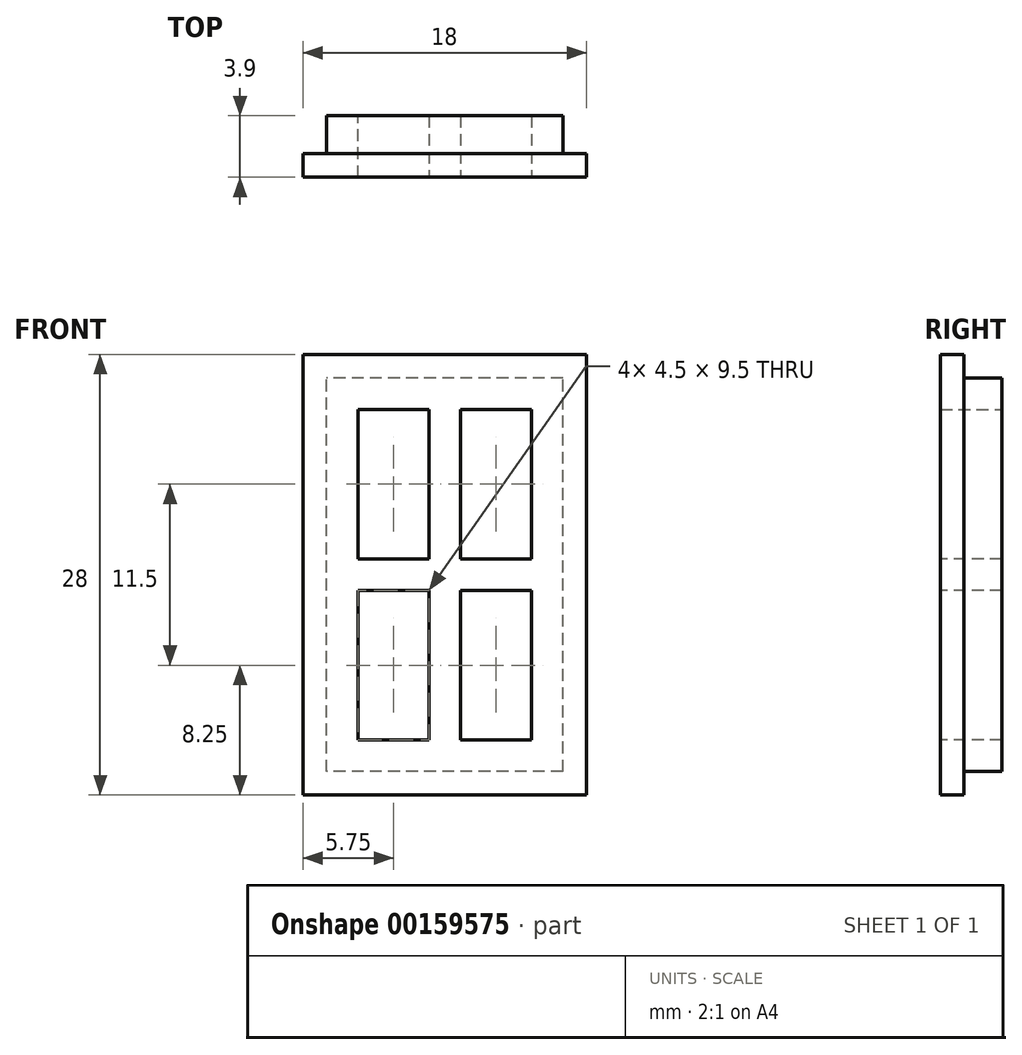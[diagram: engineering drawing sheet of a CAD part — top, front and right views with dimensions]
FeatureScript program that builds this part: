
annotation { "Feature Type Name" : "Feature", "Feature Type Description" : "" }
export const myFeature = defineFeature(function(context is Context, id is Id, definition is map)
    precondition{}
    {
        {
            var Q0;
            Q0=qCreatedBy(makeId("Front.planeOp"),FACE);
            var sketch = newSketch(context, id + "F0", { "sketchPlane" : qUnion([Q0])});
            skLineSegment(sketch, "E0.bottom", {"start": v(7.5, -12.5) * mm, "end": v(-7.5, -12.5) * mm});
            skLineSegment(sketch, "E0.top", {"start": v(7.5, 12.5) * mm, "end": v(-7.5, 12.5) * mm});
            skLineSegment(sketch, "E0.left", {"start": v(7.5, -12.5) * mm, "end": v(7.5, 12.5) * mm});
            skLineSegment(sketch, "E0.right", {"start": v(-7.5, -12.5) * mm, "end": v(-7.5, 12.5) * mm});
            skPoint(sketch, "E0.middle", {"position": v(0, 0) * mm});
            skLineSegment(sketch, "E1.0", {"start": v(5.5, -10.5) * mm, "end": v(5.5, 10.5) * mm});
            skLineSegment(sketch, "E1.1", {"start": v(5.5, -10.5) * mm, "end": v(-5.5, -10.5) * mm});
            skLineSegment(sketch, "E1.2", {"start": v(-5.5, -10.5) * mm, "end": v(-5.5, 10.5) * mm});
            skLineSegment(sketch, "E1.3", {"start": v(5.5, 10.5) * mm, "end": v(-5.5, 10.5) * mm});
            skSolve(sketch);
        }
        {
            var Q0;
            Q0=makeQuery(id+"F0.imprint","IMPRINT",FACE,{"disambiguationData":[TD([[makeQuery(id+"F0.imprint","IMPRINT",EDGE,{"derivedFrom":sQuery(id+"F0.wireOp",EDGE,"E0.bottom")}),-1.0]])]});
            extrude(context, id + "F1", {"entities" : qUnion([Q0]), "depth" : 2.4 * mm});
        }
        {
            var Q0;
            Q0=makeQuery(id+"F1.opExtrude","CAP_FACE",FACE,{"disambiguationData":[OSD([sQuery(id+"F0.wireOp",EDGE,"E0.bottom"),sQuery(id+"F0.wireOp",EDGE,"E0.top"),sQuery(id+"F0.wireOp",EDGE,"E0.left"),sQuery(id+"F0.wireOp",EDGE,"E0.right"),sQuery(id+"F0.wireOp",EDGE,"E1.0"),sQuery(id+"F0.wireOp",EDGE,"E1.1"),sQuery(id+"F0.wireOp",EDGE,"E1.2"),sQuery(id+"F0.wireOp",EDGE,"E1.3")])],"isStart":false});
            var sketch = newSketch(context, id + "F2", { "sketchPlane" : qUnion([Q0])});
            skLineSegment(sketch, "E2.0", {"start": v(5.5, 10.5) * mm, "end": v(-5.5, 10.5) * mm});
            skLineSegment(sketch, "E3.0", {"start": v(-5.5, -10.5) * mm, "end": v(-5.5, 10.5) * mm});
            skLineSegment(sketch, "E4.0", {"start": v(5.5, -10.5) * mm, "end": v(5.5, 10.5) * mm});
            skLineSegment(sketch, "E5.0", {"start": v(5.5, -10.5) * mm, "end": v(-5.5, -10.5) * mm});
            skLineSegment(sketch, "E6.bottom", {"start": v(9, -14) * mm, "end": v(-9, -14) * mm});
            skLineSegment(sketch, "E6.top", {"start": v(9, 14) * mm, "end": v(-9, 14) * mm});
            skLineSegment(sketch, "E6.left", {"start": v(9, -14) * mm, "end": v(9, 14) * mm});
            skLineSegment(sketch, "E6.right", {"start": v(-9, -14) * mm, "end": v(-9, 14) * mm});
            skPoint(sketch, "E6.middle", {"position": v(0, 0) * mm});
            skSolve(sketch);
        }
        {
            var Q0;
            Q0=makeQuery(id+"F2.imprint","IMPRINT",FACE,{"disambiguationData":[TD([[makeQuery(id+"F2.imprint","IMPRINT",EDGE,{"derivedFrom":sQuery(id+"F2.wireOp",EDGE,"E2.0")}),-1.0]])]});
            var Q1;
            Q1=makeQuery(id+"F2.imprint","IMPRINT",FACE,{"disambiguationData":[TD([[makeQuery(id+"F2.imprint","IMPRINT",EDGE,{"derivedFrom":sQuery(id+"F2.wireOp",EDGE,"E6.bottom")}),-1.0]])]});
            extrude(context, id + "F3", {"entities" : qUnion([Q0, Q1]), "operationType" : NewBodyOperationType.ADD, "depth" : 1.5 * mm});
        }
        {
            var Q0;
            Q0=makeQuery(id+"F3.opExtrude","CAP_FACE",FACE,{"disambiguationData":[OSD([sQuery(id+"F2.wireOp",EDGE,"E2.0"),sQuery(id+"F2.wireOp",EDGE,"E3.0"),sQuery(id+"F2.wireOp",EDGE,"E4.0"),sQuery(id+"F2.wireOp",EDGE,"E5.0"),sQuery(id+"F2.wireOp",EDGE,"E6.bottom"),sQuery(id+"F2.wireOp",EDGE,"E6.top"),sQuery(id+"F2.wireOp",EDGE,"E6.left"),sQuery(id+"F2.wireOp",EDGE,"E6.right")])],"isStart":false});
            var sketch = newSketch(context, id + "F4", { "sketchPlane" : qUnion([Q0])});
            skLineSegment(sketch, "E7.bottom", {"start": v(-1, 10.5) * mm, "end": v(1, 10.5) * mm});
            skLineSegment(sketch, "E7.top", {"start": v(-1, -10.5) * mm, "end": v(1, -10.5) * mm});
            skLineSegment(sketch, "E7.left", {"start": v(-1, 10.5) * mm, "end": v(-1, -10.5) * mm});
            skLineSegment(sketch, "E7.right", {"start": v(1, 10.5) * mm, "end": v(1, -10.5) * mm});
            skLineSegment(sketch, "E8.bottom", {"start": v(-5.5, 1) * mm, "end": v(5.5, 1) * mm});
            skLineSegment(sketch, "E8.top", {"start": v(-5.5, -1) * mm, "end": v(5.5, -1) * mm});
            skLineSegment(sketch, "E8.left", {"start": v(-5.5, 1) * mm, "end": v(-5.5, -1) * mm});
            skLineSegment(sketch, "E8.right", {"start": v(5.5, 1) * mm, "end": v(5.5, -1) * mm});
            skPoint(sketch, "E9", {"position": v(0, 10.5) * mm});
            skPoint(sketch, "E10", {"position": v(5.5, 0) * mm});
            skSolve(sketch);
        }
        {
            var Q0;
            {var subQ5=sQuery(id+"F4.wireOp",EDGE,"E8.left");Q0=makeQuery(id+"F4.imprint","IMPRINT",FACE,{"disambiguationData":[TD([[makeQuery(id+"F4.imprint","IMPRINT",EDGE,{"derivedFrom":subQ5}),-1.0]])]});}
            var Q1;
            {var subQ0=sQuery(id+"F4.wireOp",EDGE,"E7.bottom");Q1=makeQuery(id+"F4.imprint","IMPRINT",FACE,{"disambiguationData":[TD([[makeQuery(id+"F4.imprint","IMPRINT",EDGE,{"derivedFrom":subQ0}),1.0]])]});}
            var Q2;
            {var subQ0=sQuery(id+"F4.wireOp",EDGE,"E8.bottom");var subQ1=sQuery(id+"F4.wireOp",EDGE,"E7.left");var subQ2=makeQuery(id+"F4.imprint","INTERSECT",VERTEX,{"derivedFrom":[subQ1,subQ0]});Q2=makeQuery(id+"F4.imprint","IMPRINT",FACE,{"disambiguationData":[TD([[makeQuery(id+"F4.imprint","IMPRINT",EDGE,{"disambiguationData":[TD([[subQ2,-1.0]])],"derivedFrom":subQ1}),1.0]])]});}
            var Q3;
            {var subQ5=sQuery(id+"F4.wireOp",EDGE,"E8.right");Q3=makeQuery(id+"F4.imprint","IMPRINT",FACE,{"disambiguationData":[TD([[makeQuery(id+"F4.imprint","IMPRINT",EDGE,{"derivedFrom":subQ5}),1.0]])]});}
            var Q4;
            {var subQ0=sQuery(id+"F4.wireOp",EDGE,"E7.top");Q4=makeQuery(id+"F4.imprint","IMPRINT",FACE,{"disambiguationData":[TD([[makeQuery(id+"F4.imprint","IMPRINT",EDGE,{"derivedFrom":subQ0}),-1.0]])]});}
            extrude(context, id + "F5", {"entities" : qUnion([Q0, Q1, Q2, Q3, Q4]), "operationType" : NewBodyOperationType.ADD, "oppositeDirection" : true, "depth" : 3.9 * mm});
        }
    });
